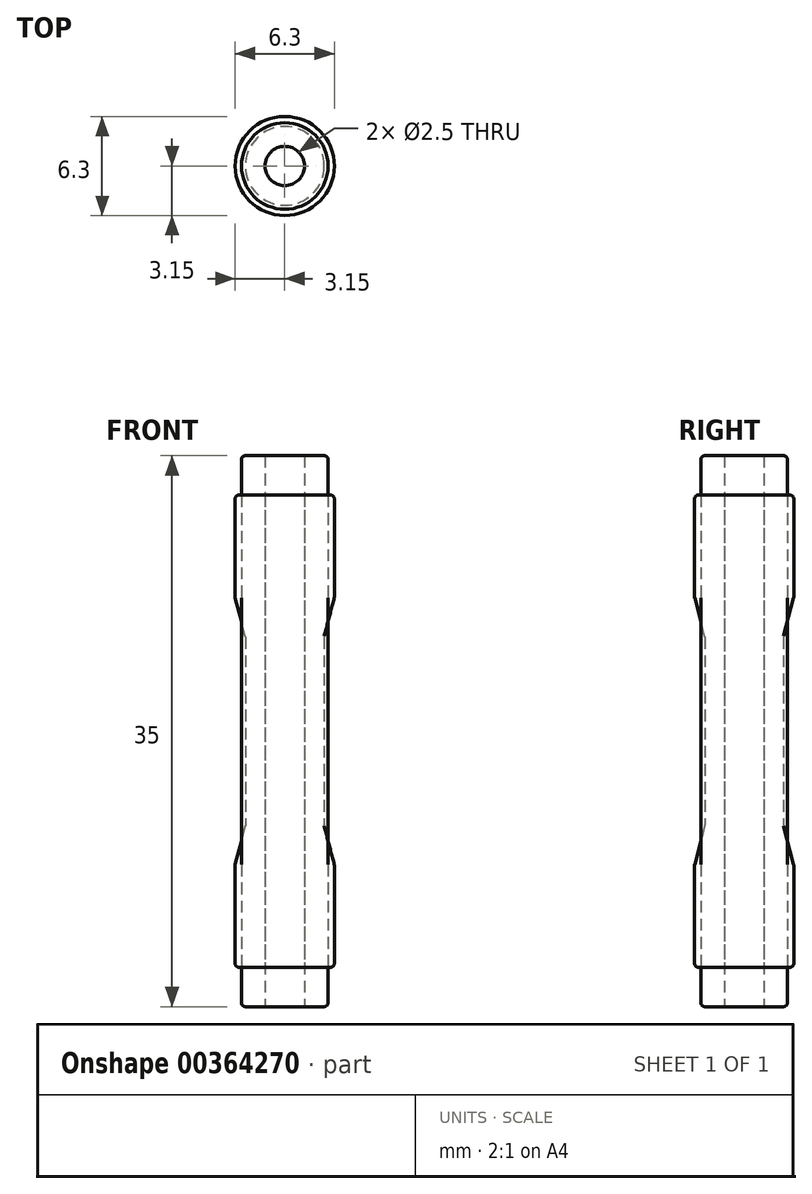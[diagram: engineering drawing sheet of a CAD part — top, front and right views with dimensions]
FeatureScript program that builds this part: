
annotation { "Feature Type Name" : "Feature", "Feature Type Description" : "" }
export const myFeature = defineFeature(function(context is Context, id is Id, definition is map)
    precondition{}
    {
        {
            var Q0;
            Q0=qCreatedBy(makeId("Front.planeOp"),FACE);
            var sketch = newSketch(context, id + "F0", { "sketchPlane" : qUnion([Q0])});
            skLineSegment(sketch, "E0", {"start": v(0, 15) * mm, "end": v(3.15, 15) * mm});
            skLineSegment(sketch, "E1", {"start": v(3.15, 15) * mm, "end": v(3.15, 8.5) * mm});
            skLineSegment(sketch, "E2", {"start": v(3.15, 8.5) * mm, "end": v(2.5, 6) * mm});
            skLineSegment(sketch, "E3", {"start": v(2.5, 6) * mm, "end": v(2.5, 0) * mm});
            skLineSegment(sketch, "E4", {"start": v(2.5, 0) * mm, "end": v(0, 0) * mm});
            skLineSegment(sketch, "E5", {"start": v(0, 0) * mm, "end": v(0, 15) * mm});
            skLineSegment(sketch, "E6", {"start": v(1.25, 15) * mm, "end": v(1.25, 0) * mm});
            skSolve(sketch);
        }
        {
            var Q0;
            {var subQ1=sQuery(id+"F0.wireOp",EDGE,"E1");Q0=makeQuery(id+"F0.imprint","IMPRINT",FACE,{"disambiguationData":[TD([[makeQuery(id+"F0.imprint","IMPRINT",EDGE,{"derivedFrom":subQ1}),-1.0]])]});}
            var Q1;
            Q1=sQuery(id+"F0.wireOp",EDGE,"E5");
            revolve(context, id + "F1", {"surfaceOperationType" : NewSurfaceOperationType.NEW, "entities" : qUnion([Q0]), "axis" : qUnion([Q1]), "revolveType" : RevolveType.FULL});
        }
        {
            var Q0;
            Q0=makeQuery(id+"F1.opRevolve","SWEPT_EDGE",EDGE,{"disambiguationData":[OSD([sQuery(id+"F0.wireOp",EDGE,"E0"),sQuery(id+"F0.wireOp",EDGE,"E1")])]});
            var Q1;
            Q1=makeQuery(id+"F1.opRevolve","SWEPT_EDGE",EDGE,{"disambiguationData":[OSD([sQuery(id+"F0.wireOp",EDGE,"E1"),sQuery(id+"F0.wireOp",EDGE,"E2")])]});
            var Q2;
            Q2=makeQuery(id+"F1.opRevolve","SWEPT_EDGE",EDGE,{"disambiguationData":[OSD([sQuery(id+"F0.wireOp",EDGE,"E2"),sQuery(id+"F0.wireOp",EDGE,"E3")])]});
            fillet(context, id + "F2", {"entities" : qUnion([Q0, Q1, Q2]), "radius" : 0.25 * mm, "tangentPropagation" : true, "allowEdgeOverflow" : false});
        }
        {
            var Q0;
            Q0=makeQuery(id+"F1.opRevolve","SWEPT_BODY",BODY,{"disambiguationData":[OSD([sQuery(id+"F0.wireOp",EDGE,"E0"),sQuery(id+"F0.wireOp",EDGE,"E1"),sQuery(id+"F0.wireOp",EDGE,"E2"),sQuery(id+"F0.wireOp",EDGE,"E3"),sQuery(id+"F0.wireOp",EDGE,"E4"),sQuery(id+"F0.wireOp",EDGE,"E6")])]});
            var Q1;
            Q1=qCreatedBy(makeId("Top.planeOp"),FACE);
            mirror(context, id + "F3", {"operationType" : NewBodyOperationType.ADD, "entities" : qUnion([Q0]), "mirrorPlane" : qUnion([Q1])});
        }
        {
            var Q0;
            Q0=qCreatedBy(makeId("Top.planeOp"),FACE);
            var sketch = newSketch(context, id + "F4", { "sketchPlane" : qUnion([Q0])});
            skCircle(sketch, "E7", {"center": v(0, 0) * mm, "radius": 2.75 * mm});
            skCircle(sketch, "E8", {"center": v(0, 0) * mm, "radius": 1.25 * mm});
            skSolve(sketch);
        }
        {
            var Q0;
            Q0=makeQuery(id+"F4.imprint","IMPRINT",FACE,{"disambiguationData":[TD([[makeQuery(id+"F4.imprint","IMPRINT",EDGE,{"derivedFrom":sQuery(id+"F4.wireOp",EDGE,"E7")}),1.0]])]});
            extrude(context, id + "F5", {"entities" : qUnion([Q0]), "endBound" : BoundingType.SYMMETRIC, "depth" : 35 * mm, "offsetDistance" : 25 * mm});
        }
        {
            var Q0;
            Q0=makeQuery(id+"F5.opExtrude","CAP_EDGE",EDGE,{"disambiguationData":[OSD([sQuery(id+"F4.wireOp",EDGE,"E7")])],"isStart":false});
            var Q1;
            Q1=makeQuery(id+"F5.opExtrude","CAP_EDGE",EDGE,{"disambiguationData":[OSD([sQuery(id+"F4.wireOp",EDGE,"E7")])],"isStart":true});
            fillet(context, id + "F6", {"entities" : qUnion([Q0, Q1]), "radius" : 0.25 * mm, "tangentPropagation" : true, "allowEdgeOverflow" : false});
        }
    });
